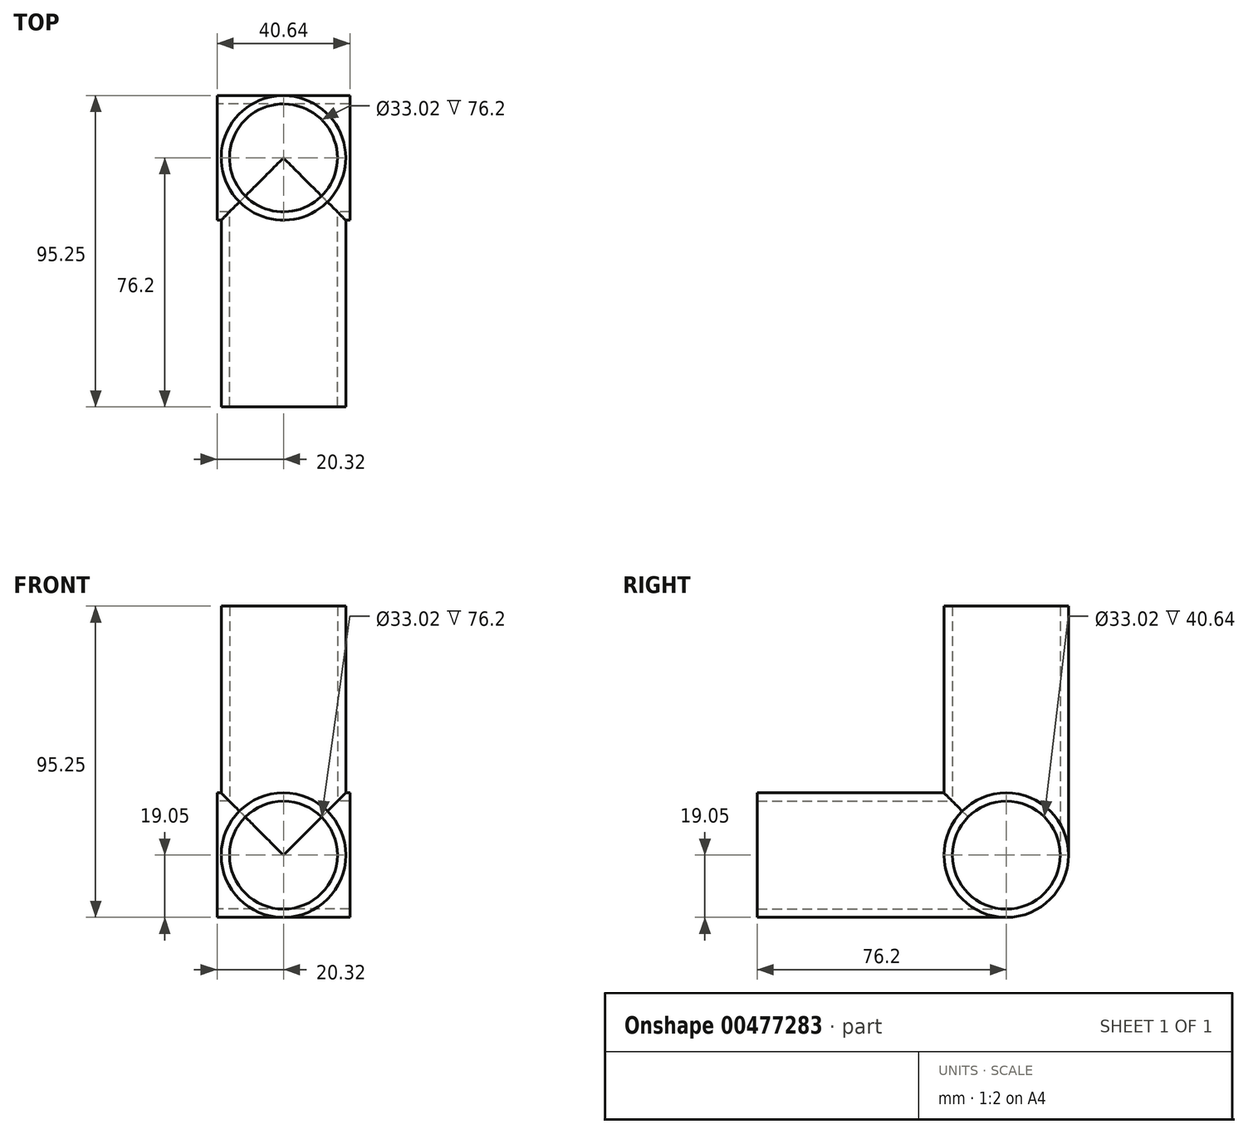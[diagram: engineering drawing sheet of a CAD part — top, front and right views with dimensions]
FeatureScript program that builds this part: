
annotation { "Feature Type Name" : "Feature", "Feature Type Description" : "" }
export const myFeature = defineFeature(function(context is Context, id is Id, definition is map)
    precondition{}
    {
        {
            var Q0;
            Q0=qCreatedBy(makeId("Front.planeOp"),FACE);
            var sketch = newSketch(context, id + "F0", { "sketchPlane" : qUnion([Q0])});
            skCircle(sketch, "E0", {"center": v(0, 0) * mm, "radius": 19.05 * mm});
            skSolve(sketch);
        }
        {
            var Q0;
            Q0=makeQuery(id+"F0.imprint","IMPRINT",FACE,{"disambiguationData":[TD([[makeQuery(id+"F0.imprint","IMPRINT",EDGE,{"derivedFrom":sQuery(id+"F0.wireOp",EDGE,"E0")}),1.0]])]});
            extrude(context, id + "F1", {"entities" : qUnion([Q0]), "depth" : 76.2 * mm});
        }
        {
            var Q0;
            Q0=qCreatedBy(makeId("Right.planeOp"),FACE);
            var sketch = newSketch(context, id + "F2", { "sketchPlane" : qUnion([Q0])});
            skCircle(sketch, "E1", {"center": v(0, 0) * mm, "radius": 19.05 * mm});
            skSolve(sketch);
        }
        {
            var Q0;
            Q0=makeQuery(id+"F2.imprint","IMPRINT",FACE,{"disambiguationData":[TD([[makeQuery(id+"F2.imprint","IMPRINT",EDGE,{"derivedFrom":sQuery(id+"F2.wireOp",EDGE,"E1")}),1.0]])]});
            extrude(context, id + "F3", {"entities" : qUnion([Q0]), "endBound" : BoundingType.SYMMETRIC, "depth" : 40.64 * mm});
        }
        {
            var Q0;
            Q0=qCreatedBy(makeId("Top.planeOp"),FACE);
            var sketch = newSketch(context, id + "F4", { "sketchPlane" : qUnion([Q0])});
            skCircle(sketch, "E2", {"center": v(0, 0) * mm, "radius": 19.05 * mm});
            skSolve(sketch);
        }
        {
            var Q0;
            Q0 = qSketchRegion(id + "F4", true);
            extrude(context, id + "F5", {"entities" : qUnion([Q0]), "operationType" : NewBodyOperationType.ADD, "depth" : 76.2 * mm});
        }
        {
            var Q0;
            Q0=sQuery(id+"F4.wireOp",VERTEX,"E2.center");
            var Q1;
            Q1=makeQuery(id+"F1.opExtrude","SWEPT_BODY",BODY,{"disambiguationData":[OSD([sQuery(id+"F0.wireOp",EDGE,"E0")])]});
            hole(context, id + "F6", {"style" : HoleStyle.SIMPLE, "endStyle" : HoleEndStyle.THROUGH, "oppositeDirection" : true, "holeDiameter" : 33.02 * mm, "isTappedThrough" : true, "tappedDepth" : 12.7 * mm, "tapClearance" : 3, "startFromSketch" : true, "locations" : qUnion([Q0]), "scope" : qUnion([Q1])});
        }
        {
            var Q0;
            Q0=sQuery(id+"F2.wireOp",VERTEX,"E1.center");
            var Q1;
            Q1=makeQuery(id+"F1.opExtrude","SWEPT_BODY",BODY,{"disambiguationData":[OSD([sQuery(id+"F0.wireOp",EDGE,"E0")])]});
            var Q2;
            Q2=makeQuery(id+"F3.opExtrude","SWEPT_BODY",BODY,{"disambiguationData":[OSD([sQuery(id+"F2.wireOp",EDGE,"E1")])]});
            hole(context, id + "F7", {"style" : HoleStyle.SIMPLE, "endStyle" : HoleEndStyle.THROUGH, "oppositeDirection" : true, "holeDiameter" : 33.02 * mm, "isTappedThrough" : true, "tappedDepth" : 12.7 * mm, "tapClearance" : 3, "startFromSketch" : true, "locations" : qUnion([Q0]), "scope" : qUnion([Q1, Q2])});
        }
        {
            var Q0;
            Q0=sQuery(id+"F2.wireOp",VERTEX,"E1.center");
            var Q1;
            Q1=makeQuery(id+"F3.opExtrude","SWEPT_BODY",BODY,{"disambiguationData":[OSD([sQuery(id+"F2.wireOp",EDGE,"E1")])]});
            var Q2;
            Q2=makeQuery(id+"F1.opExtrude","SWEPT_BODY",BODY,{"disambiguationData":[OSD([sQuery(id+"F0.wireOp",EDGE,"E0")])]});
            hole(context, id + "F8", {"style" : HoleStyle.SIMPLE, "endStyle" : HoleEndStyle.THROUGH, "holeDiameter" : 33.02 * mm, "isTappedThrough" : true, "tappedDepth" : 12.7 * mm, "tapClearance" : 3, "startFromSketch" : true, "locations" : qUnion([Q0]), "scope" : qUnion([Q1, Q2])});
        }
        {
            var Q0;
            Q0=sQuery(id+"F0.wireOp",VERTEX,"E0.center");
            var Q1;
            Q1=sQuery(id+"F4.wireOp",VERTEX,"E2.center");
            var Q2;
            Q2=makeQuery(id+"F3.opExtrude","SWEPT_BODY",BODY,{"disambiguationData":[OSD([sQuery(id+"F2.wireOp",EDGE,"E1")])]});
            var Q3;
            Q3=makeQuery(id+"F1.opExtrude","SWEPT_BODY",BODY,{"disambiguationData":[OSD([sQuery(id+"F0.wireOp",EDGE,"E0")])]});
            hole(context, id + "F9", {"style" : HoleStyle.SIMPLE, "endStyle" : HoleEndStyle.BLIND, "oppositeDirection" : true, "holeDiameter" : 33.02 * mm, "holeDepth" : 63.5 * mm, "isTappedThrough" : true, "tappedDepth" : 12.7 * mm, "tapClearance" : 3, "locations" : qUnion([Q0, Q1]), "scope" : qUnion([Q2, Q3])});
        }
    });
